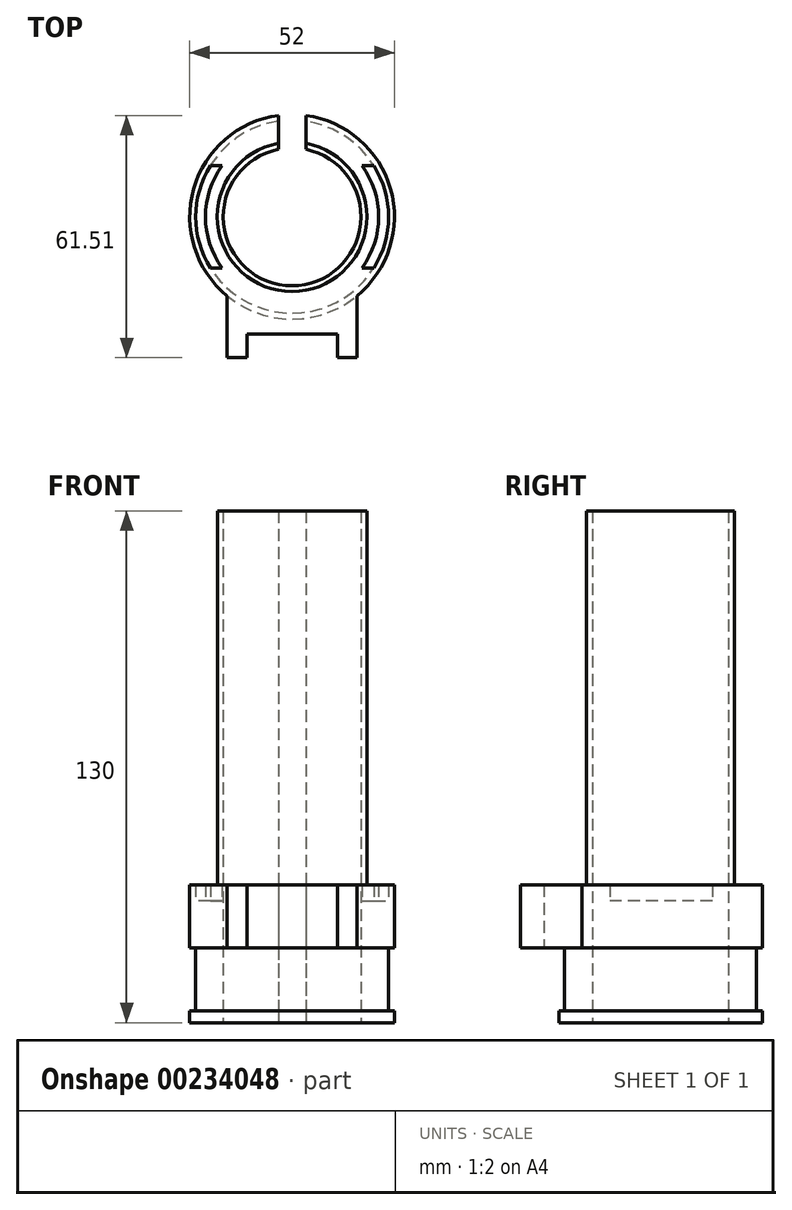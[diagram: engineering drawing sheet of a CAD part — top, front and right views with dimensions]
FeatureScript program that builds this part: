
annotation { "Feature Type Name" : "Feature", "Feature Type Description" : "" }
export const myFeature = defineFeature(function(context is Context, id is Id, definition is map)
    precondition{}
    {
        {
            var Q0;
            Q0=qCreatedBy(makeId("Top.planeOp"),FACE);
            var sketch = newSketch(context, id + "F0", { "sketchPlane" : qUnion([Q0])});
            skCircle(sketch, "E0", {"center": v(0, 0) * mm, "radius": 19 * mm});
            skCircle(sketch, "E1", {"center": v(0, 0) * mm, "radius": 17.5 * mm});
            skCircle(sketch, "E2", {"center": v(0, 0) * mm, "radius": 22 * mm});
            skCircle(sketch, "E3", {"center": v(0, 0) * mm, "radius": 24.5 * mm});
            skCircle(sketch, "E4", {"center": v(0, 0) * mm, "radius": 26 * mm});
            skLineSegment(sketch, "E5.bottom", {"start": v(-27.5, -13) * mm, "end": v(27.5, -13) * mm});
            skLineSegment(sketch, "E5.top", {"start": v(-27.5, 13) * mm, "end": v(27.5, 13) * mm});
            skLineSegment(sketch, "E5.left", {"start": v(-27.5, -13) * mm, "end": v(-27.5, 13) * mm, "construction": true});
            skLineSegment(sketch, "E5.right", {"start": v(27.5, -13) * mm, "end": v(27.5, 13) * mm, "construction": true});
            skLineSegment(sketch, "E6.bottom", {"start": v(-16.5, -35.75) * mm, "end": v(16.5, -35.75) * mm});
            skLineSegment(sketch, "E6.top", {"start": v(-16.5, -16.75) * mm, "end": v(16.5, -16.75) * mm});
            skLineSegment(sketch, "E6.left", {"start": v(-16.5, -35.75) * mm, "end": v(-16.5, -16.75) * mm});
            skLineSegment(sketch, "E6.right", {"start": v(16.5, -35.75) * mm, "end": v(16.5, -16.75) * mm});
            skLineSegment(sketch, "E7.bottom", {"start": v(-11.5, -35.75) * mm, "end": v(11.5, -35.75) * mm});
            skLineSegment(sketch, "E7.top", {"start": v(-11.5, -29.75) * mm, "end": v(11.5, -29.75) * mm});
            skLineSegment(sketch, "E7.left", {"start": v(-11.5, -35.75) * mm, "end": v(-11.5, -29.75) * mm});
            skLineSegment(sketch, "E7.right", {"start": v(11.5, -35.75) * mm, "end": v(11.5, -29.75) * mm});
            skLineSegment(sketch, "E8.bottom", {"start": v(3.5, 30) * mm, "end": v(-3.5, 30) * mm});
            skLineSegment(sketch, "E8.top", {"start": v(3.5, 0) * mm, "end": v(-3.5, 0) * mm});
            skLineSegment(sketch, "E8.left", {"start": v(3.5, 30) * mm, "end": v(3.5, 0) * mm});
            skLineSegment(sketch, "E8.right", {"start": v(-3.5, 30) * mm, "end": v(-3.5, 0) * mm});
            skSolve(sketch);
        }
        {
            var Q0;
            {var subQ0=sQuery(id+"F0.wireOp",EDGE,"E8.left");var subQ1=sQuery(id+"F0.wireOp",EDGE,"E0");var subQ2=makeQuery(id+"F0.imprint","INTERSECT",VERTEX,{"derivedFrom":[subQ1,subQ0]});Q0=makeQuery(id+"F0.imprint","IMPRINT",FACE,{"disambiguationData":[TD([[makeQuery(id+"F0.imprint","IMPRINT",EDGE,{"disambiguationData":[TD([[subQ2,1.0]])],"derivedFrom":subQ1}),1.0]])]});}
            var Q1;
            {var subQ0=sQuery(id+"F0.wireOp",EDGE,"E8.right");var subQ1=sQuery(id+"F0.wireOp",EDGE,"E0");var subQ2=makeQuery(id+"F0.imprint","INTERSECT",VERTEX,{"derivedFrom":[subQ1,subQ0]});Q1=makeQuery(id+"F0.imprint","IMPRINT",FACE,{"disambiguationData":[TD([[makeQuery(id+"F0.imprint","IMPRINT",EDGE,{"disambiguationData":[TD([[subQ2,-1.0]])],"derivedFrom":subQ1}),1.0]])]});}
            var Q2;
            {var subQ0=sQuery(id+"F0.wireOp",EDGE,"E5.top");var subQ1=sQuery(id+"F0.wireOp",EDGE,"E0");var subQ2=makeQuery(id+"F0.imprint","INTERSECT",VERTEX,{"disambiguationData":[OD(1.0)],"derivedFrom":[subQ1,subQ0]});Q2=makeQuery(id+"F0.imprint","IMPRINT",FACE,{"disambiguationData":[TD([[makeQuery(id+"F0.imprint","IMPRINT",EDGE,{"disambiguationData":[TD([[subQ2,-1.0]])],"derivedFrom":subQ1}),1.0]])]});}
            var Q3;
            {var subQ0=sQuery(id+"F0.wireOp",EDGE,"E5.bottom");var subQ1=sQuery(id+"F0.wireOp",EDGE,"E0");var subQ2=makeQuery(id+"F0.imprint","INTERSECT",VERTEX,{"disambiguationData":[OD(0.0)],"derivedFrom":[subQ1,subQ0]});Q3=makeQuery(id+"F0.imprint","IMPRINT",FACE,{"disambiguationData":[TD([[makeQuery(id+"F0.imprint","IMPRINT",EDGE,{"disambiguationData":[TD([[subQ2,-1.0]])],"derivedFrom":subQ1}),1.0]])]});}
            var Q4;
            {var subQ0=sQuery(id+"F0.wireOp",EDGE,"E6.top");var subQ1=sQuery(id+"F0.wireOp",EDGE,"E0");var subQ2=makeQuery(id+"F0.imprint","INTERSECT",VERTEX,{"disambiguationData":[OD(0.0)],"derivedFrom":[subQ1,subQ0]});Q4=makeQuery(id+"F0.imprint","IMPRINT",FACE,{"disambiguationData":[TD([[makeQuery(id+"F0.imprint","IMPRINT",EDGE,{"disambiguationData":[TD([[subQ2,-1.0]])],"derivedFrom":subQ1}),1.0]])]});}
            var Q5;
            {var subQ0=sQuery(id+"F0.wireOp",EDGE,"E6.top");var subQ1=sQuery(id+"F0.wireOp",EDGE,"E0");var subQ2=makeQuery(id+"F0.imprint","INTERSECT",VERTEX,{"disambiguationData":[OD(1.0)],"derivedFrom":[subQ1,subQ0]});Q5=makeQuery(id+"F0.imprint","IMPRINT",FACE,{"disambiguationData":[TD([[makeQuery(id+"F0.imprint","IMPRINT",EDGE,{"disambiguationData":[TD([[subQ2,-1.0]])],"derivedFrom":subQ1}),1.0]])]});}
            var Q6;
            {var subQ0=sQuery(id+"F0.wireOp",EDGE,"E5.top");var subQ1=sQuery(id+"F0.wireOp",EDGE,"E0");var subQ2=makeQuery(id+"F0.imprint","INTERSECT",VERTEX,{"disambiguationData":[OD(0.0)],"derivedFrom":[subQ1,subQ0]});Q6=makeQuery(id+"F0.imprint","IMPRINT",FACE,{"disambiguationData":[TD([[makeQuery(id+"F0.imprint","IMPRINT",EDGE,{"disambiguationData":[TD([[subQ2,1.0]])],"derivedFrom":subQ1}),1.0]])]});}
            var Q7;
            {var subQ0=sQuery(id+"F0.wireOp",EDGE,"E5.bottom");var subQ1=sQuery(id+"F0.wireOp",EDGE,"E0");var subQ2=makeQuery(id+"F0.imprint","INTERSECT",VERTEX,{"disambiguationData":[OD(0.0)],"derivedFrom":[subQ1,subQ0]});Q7=makeQuery(id+"F0.imprint","IMPRINT",FACE,{"disambiguationData":[TD([[makeQuery(id+"F0.imprint","IMPRINT",EDGE,{"disambiguationData":[TD([[subQ2,-1.0]])],"derivedFrom":subQ1}),1.0]])]});}
            var Q8;
            {var subQ0=sQuery(id+"F0.wireOp",EDGE,"E8.left");var subQ1=sQuery(id+"F0.wireOp",EDGE,"E0");var subQ2=makeQuery(id+"F0.imprint","INTERSECT",VERTEX,{"derivedFrom":[subQ1,subQ0]});Q8=makeQuery(id+"F0.imprint","IMPRINT",FACE,{"disambiguationData":[TD([[makeQuery(id+"F0.imprint","IMPRINT",EDGE,{"disambiguationData":[TD([[subQ2,1.0]])],"derivedFrom":subQ1}),1.0]])]});}
            var Q9;
            {var subQ0=sQuery(id+"F0.wireOp",EDGE,"E6.top");var subQ1=sQuery(id+"F0.wireOp",EDGE,"E0");var subQ2=makeQuery(id+"F0.imprint","INTERSECT",VERTEX,{"disambiguationData":[OD(1.0)],"derivedFrom":[subQ1,subQ0]});Q9=makeQuery(id+"F0.imprint","IMPRINT",FACE,{"disambiguationData":[TD([[makeQuery(id+"F0.imprint","IMPRINT",EDGE,{"disambiguationData":[TD([[subQ2,-1.0]])],"derivedFrom":subQ1}),1.0]])]});}
            var Q10;
            {var subQ0=sQuery(id+"F0.wireOp",EDGE,"E8.right");var subQ1=sQuery(id+"F0.wireOp",EDGE,"E0");var subQ2=makeQuery(id+"F0.imprint","INTERSECT",VERTEX,{"derivedFrom":[subQ1,subQ0]});Q10=makeQuery(id+"F0.imprint","IMPRINT",FACE,{"disambiguationData":[TD([[makeQuery(id+"F0.imprint","IMPRINT",EDGE,{"disambiguationData":[TD([[subQ2,-1.0]])],"derivedFrom":subQ1}),1.0]])]});}
            var Q11;
            {var subQ0=sQuery(id+"F0.wireOp",EDGE,"E5.top");var subQ1=sQuery(id+"F0.wireOp",EDGE,"E0");var subQ2=makeQuery(id+"F0.imprint","INTERSECT",VERTEX,{"disambiguationData":[OD(0.0)],"derivedFrom":[subQ1,subQ0]});Q11=makeQuery(id+"F0.imprint","IMPRINT",FACE,{"disambiguationData":[TD([[makeQuery(id+"F0.imprint","IMPRINT",EDGE,{"disambiguationData":[TD([[subQ2,1.0]])],"derivedFrom":subQ1}),1.0]])]});}
            var Q12;
            {var subQ0=sQuery(id+"F0.wireOp",EDGE,"E5.top");var subQ1=sQuery(id+"F0.wireOp",EDGE,"E0");var subQ2=makeQuery(id+"F0.imprint","INTERSECT",VERTEX,{"disambiguationData":[OD(1.0)],"derivedFrom":[subQ1,subQ0]});Q12=makeQuery(id+"F0.imprint","IMPRINT",FACE,{"disambiguationData":[TD([[makeQuery(id+"F0.imprint","IMPRINT",EDGE,{"disambiguationData":[TD([[subQ2,-1.0]])],"derivedFrom":subQ1}),1.0]])]});}
            extrude(context, id + "F1", {"entities" : qUnion([Q0, Q1, Q2, Q3, Q4, Q5, Q6, Q7, Q8, Q9, Q10, Q11, Q12]), "depth" : 130 * mm});
        }
        {
            var Q0;
            {var subQ0=sQuery(id+"F0.wireOp",EDGE,"E5.top");var subQ1=sQuery(id+"F0.wireOp",EDGE,"E3");var subQ2=makeQuery(id+"F0.imprint","INTERSECT",VERTEX,{"disambiguationData":[OD(0.0)],"derivedFrom":[subQ1,subQ0]});Q0=makeQuery(id+"F0.imprint","IMPRINT",FACE,{"disambiguationData":[TD([[makeQuery(id+"F0.imprint","IMPRINT",EDGE,{"disambiguationData":[TD([[subQ2,1.0]])],"derivedFrom":subQ1}),-1.0]])]});}
            var Q1;
            {var subQ0=sQuery(id+"F0.wireOp",EDGE,"E5.top");var subQ1=sQuery(id+"F0.wireOp",EDGE,"E3");var subQ2=makeQuery(id+"F0.imprint","INTERSECT",VERTEX,{"disambiguationData":[OD(0.0)],"derivedFrom":[subQ1,subQ0]});Q1=makeQuery(id+"F0.imprint","IMPRINT",FACE,{"disambiguationData":[TD([[makeQuery(id+"F0.imprint","IMPRINT",EDGE,{"disambiguationData":[TD([[subQ2,-1.0]])],"derivedFrom":subQ1}),-1.0]])]});}
            var Q2;
            {var subQ0=sQuery(id+"F0.wireOp",EDGE,"E5.bottom");var subQ1=sQuery(id+"F0.wireOp",EDGE,"E3");var subQ2=makeQuery(id+"F0.imprint","INTERSECT",VERTEX,{"disambiguationData":[OD(0.0)],"derivedFrom":[subQ1,subQ0]});Q2=makeQuery(id+"F0.imprint","IMPRINT",FACE,{"disambiguationData":[TD([[makeQuery(id+"F0.imprint","IMPRINT",EDGE,{"disambiguationData":[TD([[subQ2,-1.0]])],"derivedFrom":subQ1}),-1.0]])]});}
            var Q3;
            {var subQ0=sQuery(id+"F0.wireOp",EDGE,"E5.top");var subQ1=sQuery(id+"F0.wireOp",EDGE,"E3");var subQ2=makeQuery(id+"F0.imprint","INTERSECT",VERTEX,{"disambiguationData":[OD(1.0)],"derivedFrom":[subQ1,subQ0]});Q3=makeQuery(id+"F0.imprint","IMPRINT",FACE,{"disambiguationData":[TD([[makeQuery(id+"F0.imprint","IMPRINT",EDGE,{"disambiguationData":[TD([[subQ2,1.0]])],"derivedFrom":subQ1}),-1.0]])]});}
            var Q4;
            {var subQ0=sQuery(id+"F0.wireOp",EDGE,"E6.left");var subQ1=sQuery(id+"F0.wireOp",EDGE,"E3");var subQ2=makeQuery(id+"F0.imprint","INTERSECT",VERTEX,{"derivedFrom":[subQ1,subQ0]});Q4=makeQuery(id+"F0.imprint","IMPRINT",FACE,{"disambiguationData":[TD([[makeQuery(id+"F0.imprint","IMPRINT",EDGE,{"disambiguationData":[TD([[subQ2,-1.0]])],"derivedFrom":subQ1}),-1.0]])]});}
            var Q5;
            {var subQ0=sQuery(id+"F0.wireOp",EDGE,"E5.top");var subQ1=sQuery(id+"F0.wireOp",EDGE,"E2");var subQ2=makeQuery(id+"F0.imprint","INTERSECT",VERTEX,{"disambiguationData":[OD(0.0)],"derivedFrom":[subQ1,subQ0]});Q5=makeQuery(id+"F0.imprint","IMPRINT",FACE,{"disambiguationData":[TD([[makeQuery(id+"F0.imprint","IMPRINT",EDGE,{"disambiguationData":[TD([[subQ2,1.0]])],"derivedFrom":subQ1}),-1.0]])]});}
            var Q6;
            {var subQ0=sQuery(id+"F0.wireOp",EDGE,"E5.top");var subQ1=sQuery(id+"F0.wireOp",EDGE,"E2");var subQ2=makeQuery(id+"F0.imprint","INTERSECT",VERTEX,{"disambiguationData":[OD(0.0)],"derivedFrom":[subQ1,subQ0]});Q6=makeQuery(id+"F0.imprint","IMPRINT",FACE,{"disambiguationData":[TD([[makeQuery(id+"F0.imprint","IMPRINT",EDGE,{"disambiguationData":[TD([[subQ2,-1.0]])],"derivedFrom":subQ1}),-1.0]])]});}
            var Q7;
            {var subQ0=sQuery(id+"F0.wireOp",EDGE,"E5.top");var subQ1=sQuery(id+"F0.wireOp",EDGE,"E2");var subQ2=makeQuery(id+"F0.imprint","INTERSECT",VERTEX,{"disambiguationData":[OD(1.0)],"derivedFrom":[subQ1,subQ0]});Q7=makeQuery(id+"F0.imprint","IMPRINT",FACE,{"disambiguationData":[TD([[makeQuery(id+"F0.imprint","IMPRINT",EDGE,{"disambiguationData":[TD([[subQ2,1.0]])],"derivedFrom":subQ1}),-1.0]])]});}
            var Q8;
            {var subQ0=sQuery(id+"F0.wireOp",EDGE,"E5.top");var subQ1=sQuery(id+"F0.wireOp",EDGE,"E0");var subQ2=makeQuery(id+"F0.imprint","INTERSECT",VERTEX,{"disambiguationData":[OD(0.0)],"derivedFrom":[subQ1,subQ0]});Q8=makeQuery(id+"F0.imprint","IMPRINT",FACE,{"disambiguationData":[TD([[makeQuery(id+"F0.imprint","IMPRINT",EDGE,{"disambiguationData":[TD([[subQ2,1.0]])],"derivedFrom":subQ1}),-1.0]])]});}
            var Q9;
            {var subQ0=sQuery(id+"F0.wireOp",EDGE,"E5.top");var subQ1=sQuery(id+"F0.wireOp",EDGE,"E0");var subQ2=makeQuery(id+"F0.imprint","INTERSECT",VERTEX,{"disambiguationData":[OD(0.0)],"derivedFrom":[subQ1,subQ0]});Q9=makeQuery(id+"F0.imprint","IMPRINT",FACE,{"disambiguationData":[TD([[makeQuery(id+"F0.imprint","IMPRINT",EDGE,{"disambiguationData":[TD([[subQ2,-1.0]])],"derivedFrom":subQ1}),-1.0]])]});}
            var Q10;
            {var subQ0=sQuery(id+"F0.wireOp",EDGE,"E5.bottom");var subQ1=sQuery(id+"F0.wireOp",EDGE,"E0");var subQ2=makeQuery(id+"F0.imprint","INTERSECT",VERTEX,{"disambiguationData":[OD(0.0)],"derivedFrom":[subQ1,subQ0]});Q10=makeQuery(id+"F0.imprint","IMPRINT",FACE,{"disambiguationData":[TD([[makeQuery(id+"F0.imprint","IMPRINT",EDGE,{"disambiguationData":[TD([[subQ2,-1.0]])],"derivedFrom":subQ1}),-1.0]])]});}
            var Q11;
            {var subQ0=sQuery(id+"F0.wireOp",EDGE,"E6.top");var subQ1=sQuery(id+"F0.wireOp",EDGE,"E0");var subQ2=makeQuery(id+"F0.imprint","INTERSECT",VERTEX,{"disambiguationData":[OD(0.0)],"derivedFrom":[subQ1,subQ0]});Q11=makeQuery(id+"F0.imprint","IMPRINT",FACE,{"disambiguationData":[TD([[makeQuery(id+"F0.imprint","IMPRINT",EDGE,{"disambiguationData":[TD([[subQ2,-1.0]])],"derivedFrom":subQ1}),-1.0]])]});}
            var Q12;
            {var subQ0=sQuery(id+"F0.wireOp",EDGE,"E6.top");var subQ1=sQuery(id+"F0.wireOp",EDGE,"E0");var subQ2=makeQuery(id+"F0.imprint","INTERSECT",VERTEX,{"disambiguationData":[OD(1.0)],"derivedFrom":[subQ1,subQ0]});Q12=makeQuery(id+"F0.imprint","IMPRINT",FACE,{"disambiguationData":[TD([[makeQuery(id+"F0.imprint","IMPRINT",EDGE,{"disambiguationData":[TD([[subQ2,-1.0]])],"derivedFrom":subQ1}),-1.0]])]});}
            var Q13;
            {var subQ0=sQuery(id+"F0.wireOp",EDGE,"E5.top");var subQ1=sQuery(id+"F0.wireOp",EDGE,"E0");var subQ2=makeQuery(id+"F0.imprint","INTERSECT",VERTEX,{"disambiguationData":[OD(1.0)],"derivedFrom":[subQ1,subQ0]});Q13=makeQuery(id+"F0.imprint","IMPRINT",FACE,{"disambiguationData":[TD([[makeQuery(id+"F0.imprint","IMPRINT",EDGE,{"disambiguationData":[TD([[subQ2,1.0]])],"derivedFrom":subQ1}),-1.0]])]});}
            var Q14;
            {var subQ1=sQuery(id+"F0.wireOp",EDGE,"E6.top");var subQ3=sQuery(id+"F0.wireOp",EDGE,"E2");var subQ9=makeQuery(id+"F0.imprint","INTERSECT",VERTEX,{"disambiguationData":[OD(0.0)],"derivedFrom":[subQ3,subQ1]});Q14=makeQuery(id+"F0.imprint","IMPRINT",FACE,{"disambiguationData":[TD([[makeQuery(id+"F0.imprint","IMPRINT",EDGE,{"disambiguationData":[TD([[subQ9,-1.0]])],"derivedFrom":subQ3}),-1.0]])]});}
            var Q15;
            {var subQ0=sQuery(id+"F0.wireOp",EDGE,"E6.right");var subQ1=sQuery(id+"F0.wireOp",EDGE,"E3");var subQ2=makeQuery(id+"F0.imprint","INTERSECT",VERTEX,{"derivedFrom":[subQ1,subQ0]});Q15=makeQuery(id+"F0.imprint","IMPRINT",FACE,{"disambiguationData":[TD([[makeQuery(id+"F0.imprint","IMPRINT",EDGE,{"disambiguationData":[TD([[subQ2,-1.0]])],"derivedFrom":subQ1}),-1.0]])]});}
            var Q16;
            {var subQ1=sQuery(id+"F0.wireOp",EDGE,"E6.top");var subQ3=sQuery(id+"F0.wireOp",EDGE,"E2");var subQ4=makeQuery(id+"F0.imprint","INTERSECT",VERTEX,{"disambiguationData":[OD(1.0)],"derivedFrom":[subQ3,subQ1]});Q16=makeQuery(id+"F0.imprint","IMPRINT",FACE,{"disambiguationData":[TD([[makeQuery(id+"F0.imprint","IMPRINT",EDGE,{"disambiguationData":[TD([[subQ4,-1.0]])],"derivedFrom":subQ3}),-1.0]])]});}
            var Q17;
            {var subQ3=sQuery(id+"F0.wireOp",EDGE,"E2");var subQ5=sQuery(id+"F0.wireOp",EDGE,"E5.bottom");var subQ9=makeQuery(id+"F0.imprint","INTERSECT",VERTEX,{"disambiguationData":[OD(0.0)],"derivedFrom":[subQ3,subQ5]});Q17=makeQuery(id+"F0.imprint","IMPRINT",FACE,{"disambiguationData":[TD([[makeQuery(id+"F0.imprint","IMPRINT",EDGE,{"disambiguationData":[TD([[subQ9,-1.0]])],"derivedFrom":subQ3}),-1.0]])]});}
            var Q18;
            {var subQ0=sQuery(id+"F0.wireOp",EDGE,"E5.top");var subQ1=sQuery(id+"F0.wireOp",EDGE,"E0");var subQ2=makeQuery(id+"F0.imprint","INTERSECT",VERTEX,{"disambiguationData":[OD(1.0)],"derivedFrom":[subQ1,subQ0]});Q18=makeQuery(id+"F0.imprint","IMPRINT",FACE,{"disambiguationData":[TD([[makeQuery(id+"F0.imprint","IMPRINT",EDGE,{"disambiguationData":[TD([[subQ2,-1.0]])],"derivedFrom":subQ1}),-1.0]])]});}
            var Q19;
            {var subQ0=sQuery(id+"F0.wireOp",EDGE,"E5.top");var subQ1=sQuery(id+"F0.wireOp",EDGE,"E2");var subQ2=makeQuery(id+"F0.imprint","INTERSECT",VERTEX,{"disambiguationData":[OD(1.0)],"derivedFrom":[subQ1,subQ0]});Q19=makeQuery(id+"F0.imprint","IMPRINT",FACE,{"disambiguationData":[TD([[makeQuery(id+"F0.imprint","IMPRINT",EDGE,{"disambiguationData":[TD([[subQ2,-1.0]])],"derivedFrom":subQ1}),-1.0]])]});}
            var Q20;
            {var subQ0=sQuery(id+"F0.wireOp",EDGE,"E5.top");var subQ1=sQuery(id+"F0.wireOp",EDGE,"E3");var subQ2=makeQuery(id+"F0.imprint","INTERSECT",VERTEX,{"disambiguationData":[OD(1.0)],"derivedFrom":[subQ1,subQ0]});Q20=makeQuery(id+"F0.imprint","IMPRINT",FACE,{"disambiguationData":[TD([[makeQuery(id+"F0.imprint","IMPRINT",EDGE,{"disambiguationData":[TD([[subQ2,-1.0]])],"derivedFrom":subQ1}),-1.0]])]});}
            extrude(context, id + "F2", {"entities" : qUnion([Q0, Q1, Q2, Q3, Q4, Q5, Q6, Q7, Q8, Q9, Q10, Q11, Q12, Q13, Q14, Q15, Q16, Q17, Q18, Q19, Q20]), "operationType" : NewBodyOperationType.ADD, "depth" : 35 * mm});
        }
        {
            var Q0;
            {var subQ0=sQuery(id+"F0.wireOp",EDGE,"E5.top");var subQ1=sQuery(id+"F0.wireOp",EDGE,"E2");var subQ2=makeQuery(id+"F0.imprint","INTERSECT",VERTEX,{"disambiguationData":[OD(0.0)],"derivedFrom":[subQ1,subQ0]});Q0=makeQuery(id+"F0.imprint","IMPRINT",FACE,{"disambiguationData":[TD([[makeQuery(id+"F0.imprint","IMPRINT",EDGE,{"disambiguationData":[TD([[subQ2,1.0]])],"derivedFrom":subQ1}),-1.0]])]});}
            var Q1;
            {var subQ0=sQuery(id+"F0.wireOp",EDGE,"E5.top");var subQ1=sQuery(id+"F0.wireOp",EDGE,"E2");var subQ2=makeQuery(id+"F0.imprint","INTERSECT",VERTEX,{"disambiguationData":[OD(1.0)],"derivedFrom":[subQ1,subQ0]});Q1=makeQuery(id+"F0.imprint","IMPRINT",FACE,{"disambiguationData":[TD([[makeQuery(id+"F0.imprint","IMPRINT",EDGE,{"disambiguationData":[TD([[subQ2,-1.0]])],"derivedFrom":subQ1}),-1.0]])]});}
            extrude(context, id + "F3", {"entities" : qUnion([Q0, Q1]), "operationType" : NewBodyOperationType.REMOVE, "depth" : 35 * mm, "hasSecondDirection" : true, "secondDirectionOppositeDirection" : false, "secondDirectionDepth" : 31 * mm});
        }
        {
            var Q0;
            Q0=makeQuery(id+"F0.imprint","IMPRINT",FACE,{"disambiguationData":[TD([[makeQuery(id+"F0.imprint","IMPRINT",EDGE,{"derivedFrom":sQuery(id+"F0.wireOp",EDGE,"E7.top")}),1.0]])]});
            extrude(context, id + "F4", {"entities" : qUnion([Q0]), "operationType" : NewBodyOperationType.ADD, "depth" : 35 * mm, "hasSecondDirection" : true, "secondDirectionOppositeDirection" : false, "secondDirectionDepth" : 19 * mm});
        }
        {
            var Q0;
            {var subQ0=sQuery(id+"F0.wireOp",EDGE,"E5.top");var subQ1=sQuery(id+"F0.wireOp",EDGE,"E3");var subQ2=makeQuery(id+"F0.imprint","INTERSECT",VERTEX,{"disambiguationData":[OD(0.0)],"derivedFrom":[subQ1,subQ0]});Q0=makeQuery(id+"F0.imprint","IMPRINT",FACE,{"disambiguationData":[TD([[makeQuery(id+"F0.imprint","IMPRINT",EDGE,{"disambiguationData":[TD([[subQ2,1.0]])],"derivedFrom":subQ1}),-1.0]])]});}
            var Q1;
            {var subQ0=sQuery(id+"F0.wireOp",EDGE,"E5.top");var subQ1=sQuery(id+"F0.wireOp",EDGE,"E3");var subQ2=makeQuery(id+"F0.imprint","INTERSECT",VERTEX,{"disambiguationData":[OD(0.0)],"derivedFrom":[subQ1,subQ0]});Q1=makeQuery(id+"F0.imprint","IMPRINT",FACE,{"disambiguationData":[TD([[makeQuery(id+"F0.imprint","IMPRINT",EDGE,{"disambiguationData":[TD([[subQ2,-1.0]])],"derivedFrom":subQ1}),-1.0]])]});}
            var Q2;
            {var subQ0=sQuery(id+"F0.wireOp",EDGE,"E5.bottom");var subQ1=sQuery(id+"F0.wireOp",EDGE,"E3");var subQ2=makeQuery(id+"F0.imprint","INTERSECT",VERTEX,{"disambiguationData":[OD(0.0)],"derivedFrom":[subQ1,subQ0]});Q2=makeQuery(id+"F0.imprint","IMPRINT",FACE,{"disambiguationData":[TD([[makeQuery(id+"F0.imprint","IMPRINT",EDGE,{"disambiguationData":[TD([[subQ2,-1.0]])],"derivedFrom":subQ1}),-1.0]])]});}
            var Q3;
            {var subQ0=sQuery(id+"F0.wireOp",EDGE,"E6.left");var subQ1=sQuery(id+"F0.wireOp",EDGE,"E3");var subQ2=makeQuery(id+"F0.imprint","INTERSECT",VERTEX,{"derivedFrom":[subQ1,subQ0]});Q3=makeQuery(id+"F0.imprint","IMPRINT",FACE,{"disambiguationData":[TD([[makeQuery(id+"F0.imprint","IMPRINT",EDGE,{"disambiguationData":[TD([[subQ2,-1.0]])],"derivedFrom":subQ1}),-1.0]])]});}
            var Q4;
            {var subQ0=sQuery(id+"F0.wireOp",EDGE,"E6.right");var subQ1=sQuery(id+"F0.wireOp",EDGE,"E3");var subQ2=makeQuery(id+"F0.imprint","INTERSECT",VERTEX,{"derivedFrom":[subQ1,subQ0]});Q4=makeQuery(id+"F0.imprint","IMPRINT",FACE,{"disambiguationData":[TD([[makeQuery(id+"F0.imprint","IMPRINT",EDGE,{"disambiguationData":[TD([[subQ2,-1.0]])],"derivedFrom":subQ1}),-1.0]])]});}
            var Q5;
            {var subQ0=sQuery(id+"F0.wireOp",EDGE,"E5.top");var subQ1=sQuery(id+"F0.wireOp",EDGE,"E3");var subQ2=makeQuery(id+"F0.imprint","INTERSECT",VERTEX,{"disambiguationData":[OD(1.0)],"derivedFrom":[subQ1,subQ0]});Q5=makeQuery(id+"F0.imprint","IMPRINT",FACE,{"disambiguationData":[TD([[makeQuery(id+"F0.imprint","IMPRINT",EDGE,{"disambiguationData":[TD([[subQ2,1.0]])],"derivedFrom":subQ1}),-1.0]])]});}
            var Q6;
            {var subQ0=sQuery(id+"F0.wireOp",EDGE,"E5.top");var subQ1=sQuery(id+"F0.wireOp",EDGE,"E3");var subQ2=makeQuery(id+"F0.imprint","INTERSECT",VERTEX,{"disambiguationData":[OD(1.0)],"derivedFrom":[subQ1,subQ0]});Q6=makeQuery(id+"F0.imprint","IMPRINT",FACE,{"disambiguationData":[TD([[makeQuery(id+"F0.imprint","IMPRINT",EDGE,{"disambiguationData":[TD([[subQ2,-1.0]])],"derivedFrom":subQ1}),-1.0]])]});}
            extrude(context, id + "F5", {"entities" : qUnion([Q0, Q1, Q2, Q3, Q4, Q5, Q6]), "operationType" : NewBodyOperationType.REMOVE, "depth" : 19 * mm, "hasSecondDirection" : true, "secondDirectionOppositeDirection" : false, "secondDirectionDepth" : 3 * mm});
        }
    });
